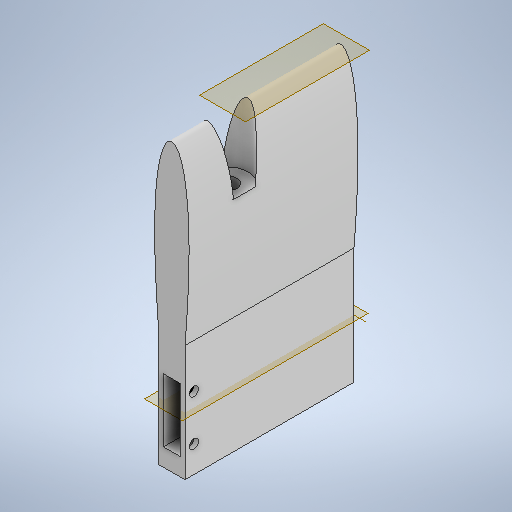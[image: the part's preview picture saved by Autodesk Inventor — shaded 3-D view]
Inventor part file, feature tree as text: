
AUTODESK INVENTOR PART (.ipt)
format: ipt  version: 2025.2 (Build 292293000, 293)  size: 388,608 bytes
history: native  units: in
note: dims shown in document units (in); Inventor stores cm internally (conversion verified against a paired STEP export)
features: extrude x10, sketch x10, other x7, plane x5, projected_geometry x2, mirror x1
ambient origin geometry x8: Origin, YZ Plane, XZ Plane, XY Plane, X Axis, Y Axis, Z Axis, Center Point
bodies: Solid1 (feature_tree)
feature tree (35):
  plane  "Work Plane1"
  extrude  "Extrusion1"  Depth=4.7244in TaperAngle=0.0deg
  plane  "Work Plane3"
  other  "Work Axis1"
  plane  "Work Plane4"
  other  "Work Point1"
  extrude  "Extrusion2"  Depth=1.8899in TaperAngle=0.0deg
  other  "Work Axis2"
  plane  "Work Plane5"
  extrude  "Extrusion7"  Depth=0.5in
  extrude  "Extrusion8"  Depth=4.272in TaperAngle=0.0deg
  extrude  "Extrusion9"  Depth=4.7865in TaperAngle=0.0deg
  extrude  "Extrusion10"  Depth=2.2658in
  extrude  "Extrusion11"  Depth=0.906in
  plane  "Work Plane6"
  mirror  "Mirror1"
  extrude  "Extrusion12"  Depth=1.084in TaperAngle=0.0deg
  extrude  "Extrusion13"  Depth=0.2559in TaperAngle=0.0deg
  extrude  "Extrusion14"  Depth=0.25in
  sketch  "Sketch1"  dims[d2=8.0in d3=4.7244in d4=0.0in]
  sketch  "Sketch3"  dims[d8=1.125in d11=1.8899in d12=0.0in]
  sketch  "Sketch9"  dims[d15=13.0in d16=0.5in]
  sketch  "Sketch10"  dims[d33=0.4724in d37=4.272in d38=0.0in]
  projected_geometry  "Projected Loop2"
  sketch  "Sketch11"  dims[d39=0.5in d40=4.7865in d41=0.0in]
  projected_geometry  "Projected Loop3"
  sketch  "Sketch12"  dims[d42=1.7717in d44=2.2658in]
  sketch  "Sketch13"  dims[d45=0.4724in d46=0.906in]
  other  "Work Axis3"
  sketch  "Sketch14"  dims[d47=2.081in d48=1.084in d49=0.0in]
  sketch  "Sketch16"  dims[d50=1.22in d51=0.2559in d52=0.0in]
  sketch  "Sketch17"  dims[d53=0.0984in d54=0.0984in d55=0.0787in d56=0.0787in d57=0.0787in d58=0.0787in d59=0.8661in d60=0.0in d61=90.0deg d62=0.25in d63=0.25in d64=0.25in d66=1.0in d68=1.8675in d69=4.735in d70=1.0in d71=0.0in d72=0.25in d73=0.744in d74=0.25in d75=0.25in d76=0.0in d77=0.25in d78=1.272in d79=0.25in d80=0.25in d81=0.0in d13=0.5in d14=0.0344in d82=0.5in d83=0.0344in d84=0.5in d85=0.0344in]
  other  "<userpath>\OneDrive\Documents\Spring 2025\Senior Design\Tail\TailAssembly.iam"
  other  "TailAssembly.iam"
  other  "MiddleTailLeft:1"
